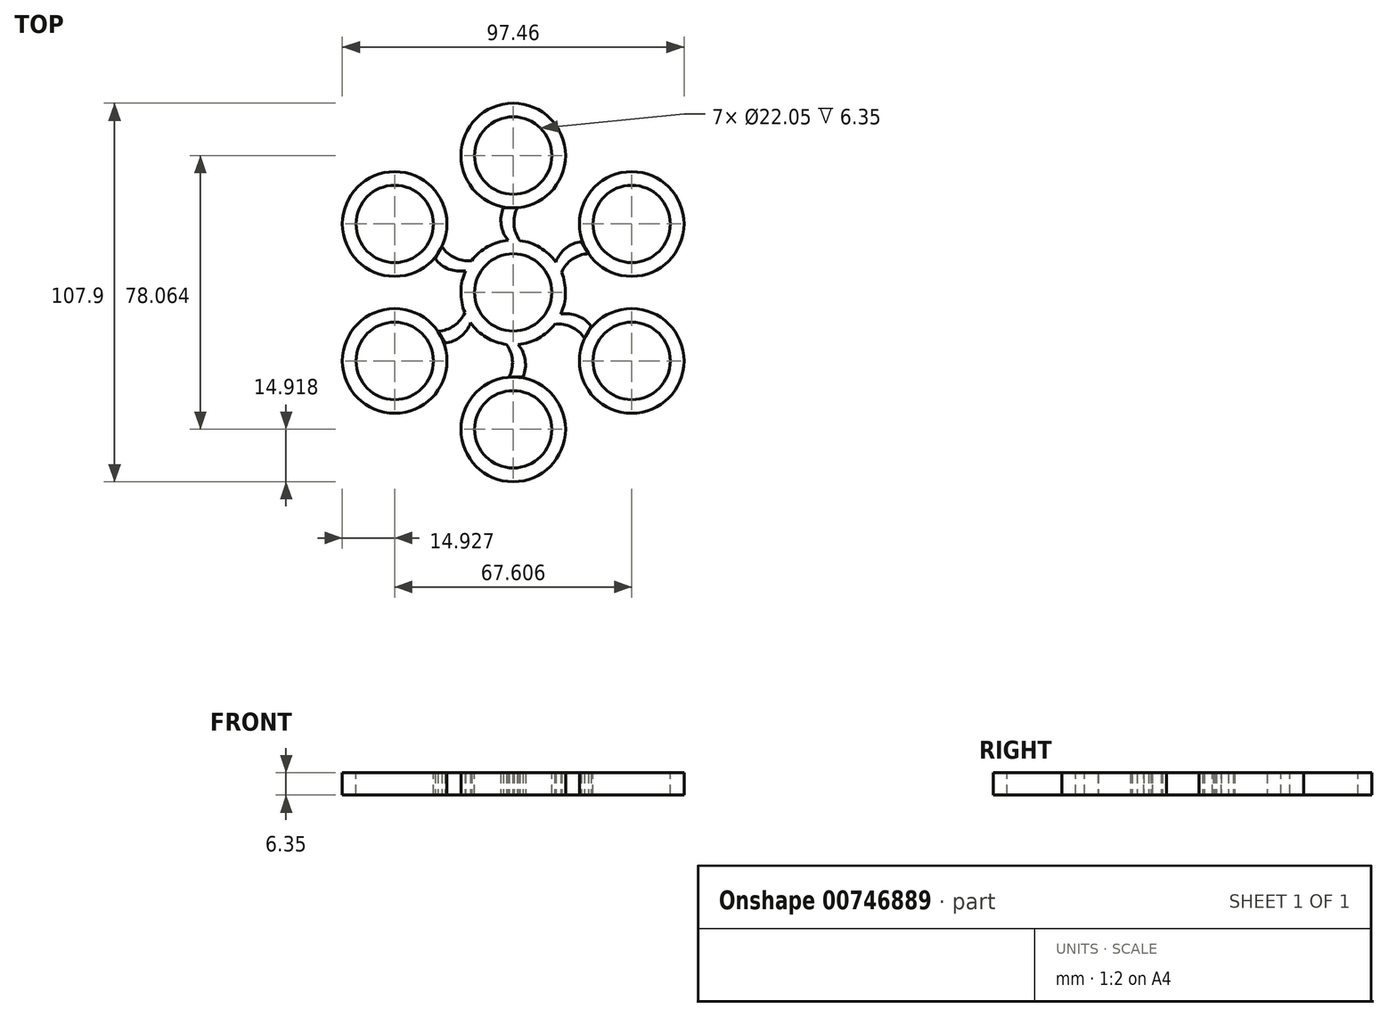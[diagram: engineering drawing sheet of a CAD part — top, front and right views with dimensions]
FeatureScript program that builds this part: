
annotation { "Feature Type Name" : "Feature", "Feature Type Description" : "" }
export const myFeature = defineFeature(function(context is Context, id is Id, definition is map)
    precondition{}
    {
        {
            var Q0;
            Q0=qCreatedBy(makeId("Top.planeOp"),FACE);
            var sketch = newSketch(context, id + "F0", { "sketchPlane" : qUnion([Q0])});
            skCircle(sketch, "E0", {"center": v(0, 0) * mm, "radius": 14.92 * mm});
            skArc(sketch, "E1", {"start": v(-2.78, 24.1) * mm, "mid": v(-3.42, 19.29) * mm, "end": v(-1.45, 14.85) * mm});
            skArc(sketch, "E2", {"start": v(1.15, 24.1) * mm, "mid": v(0.22, 19.34) * mm, "end": v(1.92, 14.8) * mm});
            skLineSegment(sketch, "E3", {"start": v(-2.78, 24.1) * mm, "end": v(1.15, 24.1) * mm});
            skLineSegment(sketch, "E4", {"start": v(-1.45, 14.85) * mm, "end": v(1.92, 14.8) * mm});
            skLineSegment(sketch, "E5.1.0", {"start": v(-22.26, 9.64) * mm, "end": v(-20.3, 13.05) * mm});
            skArc(sketch, "E5.1.1", {"start": v(-22.26, 9.64) * mm, "mid": v(-18.41, 6.68) * mm, "end": v(-13.59, 6.17) * mm});
            skArc(sketch, "E5.1.2", {"start": v(-20.3, 13.05) * mm, "mid": v(-16.64, 9.86) * mm, "end": v(-11.85, 9.06) * mm});
            skLineSegment(sketch, "E5.2.0", {"start": v(-19.48, -14.46) * mm, "end": v(-21.45, -11.05) * mm});
            skArc(sketch, "E5.2.1", {"start": v(-19.48, -14.46) * mm, "mid": v(-15, -12.6) * mm, "end": v(-12.14, -8.68) * mm});
            skArc(sketch, "E5.2.2", {"start": v(-21.45, -11.05) * mm, "mid": v(-16.86, -9.48) * mm, "end": v(-13.78, -5.73) * mm});
            skLineSegment(sketch, "E5.3.0", {"start": v(2.78, -24.1) * mm, "end": v(-1.15, -24.1) * mm});
            skArc(sketch, "E5.3.1", {"start": v(2.78, -24.1) * mm, "mid": v(3.42, -19.29) * mm, "end": v(1.45, -14.85) * mm});
            skArc(sketch, "E5.3.2", {"start": v(-1.15, -24.1) * mm, "mid": v(-0.22, -19.34) * mm, "end": v(-1.92, -14.8) * mm});
            skLineSegment(sketch, "E5.4.0", {"start": v(22.26, -9.64) * mm, "end": v(20.3, -13.05) * mm});
            skArc(sketch, "E5.4.1", {"start": v(22.26, -9.64) * mm, "mid": v(18.41, -6.68) * mm, "end": v(13.59, -6.17) * mm});
            skArc(sketch, "E5.4.2", {"start": v(20.3, -13.05) * mm, "mid": v(16.64, -9.86) * mm, "end": v(11.85, -9.06) * mm});
            skLineSegment(sketch, "E5.5.0", {"start": v(19.48, 14.46) * mm, "end": v(21.45, 11.05) * mm});
            skArc(sketch, "E5.5.1", {"start": v(19.48, 14.46) * mm, "mid": v(15, 12.6) * mm, "end": v(12.14, 8.68) * mm});
            skArc(sketch, "E5.5.2", {"start": v(21.45, 11.05) * mm, "mid": v(16.86, 9.48) * mm, "end": v(13.78, 5.73) * mm});
            skCircle(sketch, "E6", {"center": v(0, 39.03) * mm, "radius": 14.92 * mm});
            skCircle(sketch, "E7.1.0", {"center": v(-33.8, 19.52) * mm, "radius": 14.92 * mm});
            skCircle(sketch, "E7.2.0", {"center": v(-33.8, -19.52) * mm, "radius": 14.92 * mm});
            skCircle(sketch, "E7.3.0", {"center": v(0, -39.03) * mm, "radius": 14.92 * mm});
            skCircle(sketch, "E7.4.0", {"center": v(33.8, -19.52) * mm, "radius": 14.92 * mm});
            skCircle(sketch, "E7.5.0", {"center": v(33.8, 19.52) * mm, "radius": 14.92 * mm});
            skSolve(sketch);
        }
        {
            var Q0;
            Q0 = qSketchRegion(id + "F0", true);
            extrude(context, id + "F1", {"entities" : qUnion([Q0]), "depth" : 6.35 * mm, "offsetDistance" : 25.4 * mm});
        }
        {
            var Q0;
            Q0=makeQuery(id+"F1.opExtrude","CAP_FACE",FACE,{"disambiguationData":[OSD([sQuery(id+"F0.wireOp",EDGE,"E7.1.0")])],"isStart":false});
            var sketch = newSketch(context, id + "F2", { "sketchPlane" : qUnion([Q0])});
            skCircle(sketch, "E8", {"center": v(-33.8, 19.52) * mm, "radius": 11.02 * mm});
            skCircle(sketch, "E9.1.0", {"center": v(-33.8, -19.52) * mm, "radius": 11.02 * mm});
            skCircle(sketch, "E9.2.0", {"center": v(0, -39.03) * mm, "radius": 11.02 * mm});
            skCircle(sketch, "E9.3.0", {"center": v(33.8, -19.52) * mm, "radius": 11.02 * mm});
            skCircle(sketch, "E9.4.0", {"center": v(33.8, 19.52) * mm, "radius": 11.02 * mm});
            skCircle(sketch, "E9.5.0", {"center": v(0, 39.03) * mm, "radius": 11.02 * mm});
            skPoint(sketch, "E9.center", {"position": v(0, 0) * mm});
            skSolve(sketch);
        }
        {
            var Q0;
            Q0=makeQuery(id+"F2.imprint","IMPRINT",FACE,{"disambiguationData":[TD([[makeQuery(id+"F2.imprint","IMPRINT",EDGE,{"derivedFrom":sQuery(id+"F2.wireOp",EDGE,"E8")}),1.0]])]});
            var Q1;
            Q1=makeQuery(id+"F2.imprint","IMPRINT",FACE,{"disambiguationData":[TD([[makeQuery(id+"F2.imprint","IMPRINT",EDGE,{"derivedFrom":sQuery(id+"F2.wireOp",EDGE,"E9.5.0")}),1.0]])]});
            var Q2;
            Q2=makeQuery(id+"F2.imprint","IMPRINT",FACE,{"disambiguationData":[TD([[makeQuery(id+"F2.imprint","IMPRINT",EDGE,{"derivedFrom":sQuery(id+"F2.wireOp",EDGE,"E9.4.0")}),1.0]])]});
            var Q3;
            Q3=makeQuery(id+"F2.imprint","IMPRINT",FACE,{"disambiguationData":[TD([[makeQuery(id+"F2.imprint","IMPRINT",EDGE,{"derivedFrom":sQuery(id+"F2.wireOp",EDGE,"E9.3.0")}),1.0]])]});
            var Q4;
            Q4=makeQuery(id+"F2.imprint","IMPRINT",FACE,{"disambiguationData":[TD([[makeQuery(id+"F2.imprint","IMPRINT",EDGE,{"derivedFrom":sQuery(id+"F2.wireOp",EDGE,"E9.2.0")}),1.0]])]});
            var Q5;
            Q5=makeQuery(id+"F2.imprint","IMPRINT",FACE,{"disambiguationData":[TD([[makeQuery(id+"F2.imprint","IMPRINT",EDGE,{"derivedFrom":sQuery(id+"F2.wireOp",EDGE,"E9.1.0")}),1.0]])]});
            extrude(context, id + "F3", {"entities" : qUnion([Q0, Q1, Q2, Q3, Q4, Q5]), "operationType" : NewBodyOperationType.REMOVE, "oppositeDirection" : true, "depth" : 25.4 * mm, "offsetDistance" : 25.4 * mm});
        }
        {
            var Q0;
            Q0=makeQuery(id+"F1.opExtrude","CAP_FACE",FACE,{"disambiguationData":[OSD([sQuery(id+"F0.wireOp",EDGE,"E6")])],"isStart":false});
            var sketch = newSketch(context, id + "F4", { "sketchPlane" : qUnion([Q0])});
            skCircle(sketch, "E10", {"center": v(0, 39.03) * mm, "radius": 11.02 * mm});
            skSolve(sketch);
        }
        {
            var Q0;
            Q0=makeQuery(id+"F1.opExtrude","CAP_FACE",FACE,{"disambiguationData":[OSD([sQuery(id+"F0.wireOp",EDGE,"E7.5.0")])],"isStart":false});
            var sketch = newSketch(context, id + "F5", { "sketchPlane" : qUnion([Q0])});
            skCircle(sketch, "E11", {"center": v(33.8, 19.52) * mm, "radius": 11.02 * mm});
            skSolve(sketch);
        }
        {
            var Q0;
            Q0=makeQuery(id+"F1.opExtrude","CAP_FACE",FACE,{"disambiguationData":[OSD([sQuery(id+"F0.wireOp",EDGE,"E7.4.0")])],"isStart":false});
            var sketch = newSketch(context, id + "F6", { "sketchPlane" : qUnion([Q0])});
            skCircle(sketch, "E12", {"center": v(33.8, -19.52) * mm, "radius": 11.02 * mm});
            skSolve(sketch);
        }
        {
            var Q0;
            Q0=makeQuery(id+"F1.opExtrude","CAP_FACE",FACE,{"disambiguationData":[OSD([sQuery(id+"F0.wireOp",EDGE,"E7.3.0")])],"isStart":false});
            var sketch = newSketch(context, id + "F7", { "sketchPlane" : qUnion([Q0])});
            skCircle(sketch, "E13", {"center": v(0, -39.03) * mm, "radius": 11.02 * mm});
            skSolve(sketch);
        }
        {
            var Q0;
            Q0=makeQuery(id+"F1.opExtrude","CAP_FACE",FACE,{"disambiguationData":[OSD([sQuery(id+"F0.wireOp",EDGE,"E7.2.0")])],"isStart":false});
            var sketch = newSketch(context, id + "F8", { "sketchPlane" : qUnion([Q0])});
            skCircle(sketch, "E14", {"center": v(-33.8, -19.52) * mm, "radius": 11.02 * mm});
            skSolve(sketch);
        }
        {
            var Q0;
            Q0=makeQuery(id+"F4.imprint","IMPRINT",FACE,{"disambiguationData":[TD([[makeQuery(id+"F4.imprint","IMPRINT",EDGE,{"derivedFrom":sQuery(id+"F4.wireOp",EDGE,"E10")}),1.0]])]});
            extrude(context, id + "F9", {"entities" : qUnion([Q0]), "operationType" : NewBodyOperationType.REMOVE, "oppositeDirection" : true, "depth" : 25.4 * mm, "offsetDistance" : 25.4 * mm});
        }
        {
            var Q0;
            Q0=makeQuery(id+"F5.imprint","IMPRINT",FACE,{"disambiguationData":[TD([[makeQuery(id+"F5.imprint","IMPRINT",EDGE,{"derivedFrom":sQuery(id+"F5.wireOp",EDGE,"E11")}),1.0]])]});
            extrude(context, id + "F10", {"entities" : qUnion([Q0]), "operationType" : NewBodyOperationType.REMOVE, "oppositeDirection" : true, "depth" : 25.4 * mm, "offsetDistance" : 25.4 * mm});
        }
        {
            var Q0;
            Q0=makeQuery(id+"F6.imprint","IMPRINT",FACE,{"disambiguationData":[TD([[makeQuery(id+"F6.imprint","IMPRINT",EDGE,{"derivedFrom":sQuery(id+"F6.wireOp",EDGE,"E12")}),1.0]])]});
            extrude(context, id + "F11", {"entities" : qUnion([Q0]), "operationType" : NewBodyOperationType.REMOVE, "oppositeDirection" : true, "depth" : 25.4 * mm, "offsetDistance" : 25.4 * mm});
        }
        {
            var Q0;
            Q0=makeQuery(id+"F7.imprint","IMPRINT",FACE,{"disambiguationData":[TD([[makeQuery(id+"F7.imprint","IMPRINT",EDGE,{"derivedFrom":sQuery(id+"F7.wireOp",EDGE,"E13")}),1.0]])]});
            extrude(context, id + "F12", {"entities" : qUnion([Q0]), "operationType" : NewBodyOperationType.REMOVE, "oppositeDirection" : true, "depth" : 25.4 * mm, "offsetDistance" : 25.4 * mm});
        }
        {
            var Q0;
            Q0=makeQuery(id+"F8.imprint","IMPRINT",FACE,{"disambiguationData":[TD([[makeQuery(id+"F8.imprint","IMPRINT",EDGE,{"derivedFrom":sQuery(id+"F8.wireOp",EDGE,"E14")}),1.0]])]});
            extrude(context, id + "F13", {"entities" : qUnion([Q0]), "operationType" : NewBodyOperationType.REMOVE, "oppositeDirection" : true, "depth" : 25.4 * mm, "offsetDistance" : 25.4 * mm});
        }
        {
            var Q0;
            Q0=makeQuery(id+"F1.opExtrude","CAP_FACE",FACE,{"disambiguationData":[OSD([sQuery(id+"F0.wireOp",EDGE,"E1"),sQuery(id+"F0.wireOp",EDGE,"E2"),sQuery(id+"F0.wireOp",EDGE,"E3"),sQuery(id+"F0.wireOp",EDGE,"E5.1.0"),sQuery(id+"F0.wireOp",EDGE,"E5.1.1"),sQuery(id+"F0.wireOp",EDGE,"E5.1.2"),sQuery(id+"F0.wireOp",EDGE,"E5.2.0"),sQuery(id+"F0.wireOp",EDGE,"E5.2.1"),sQuery(id+"F0.wireOp",EDGE,"E5.2.2"),sQuery(id+"F0.wireOp",EDGE,"E5.3.0"),sQuery(id+"F0.wireOp",EDGE,"E5.3.1"),sQuery(id+"F0.wireOp",EDGE,"E5.3.2"),sQuery(id+"F0.wireOp",EDGE,"E5.4.0"),sQuery(id+"F0.wireOp",EDGE,"E5.4.1"),sQuery(id+"F0.wireOp",EDGE,"E5.4.2"),sQuery(id+"F0.wireOp",EDGE,"E5.5.0"),sQuery(id+"F0.wireOp",EDGE,"E5.5.1"),sQuery(id+"F0.wireOp",EDGE,"E5.5.2"),sQuery(id+"F0.wireOp",EDGE,"E0")])],"isStart":false});
            var sketch = newSketch(context, id + "F14", { "sketchPlane" : qUnion([Q0])});
            skCircle(sketch, "E15", {"center": v(0, 0) * mm, "radius": 11.02 * mm});
            skSolve(sketch);
        }
        {
            var Q0;
            Q0 = qSketchRegion(id + "F14", true);
            extrude(context, id + "F15", {"entities" : qUnion([Q0]), "operationType" : NewBodyOperationType.REMOVE, "oppositeDirection" : true, "depth" : 25.4 * mm, "offsetDistance" : 25.4 * mm});
        }
    });
